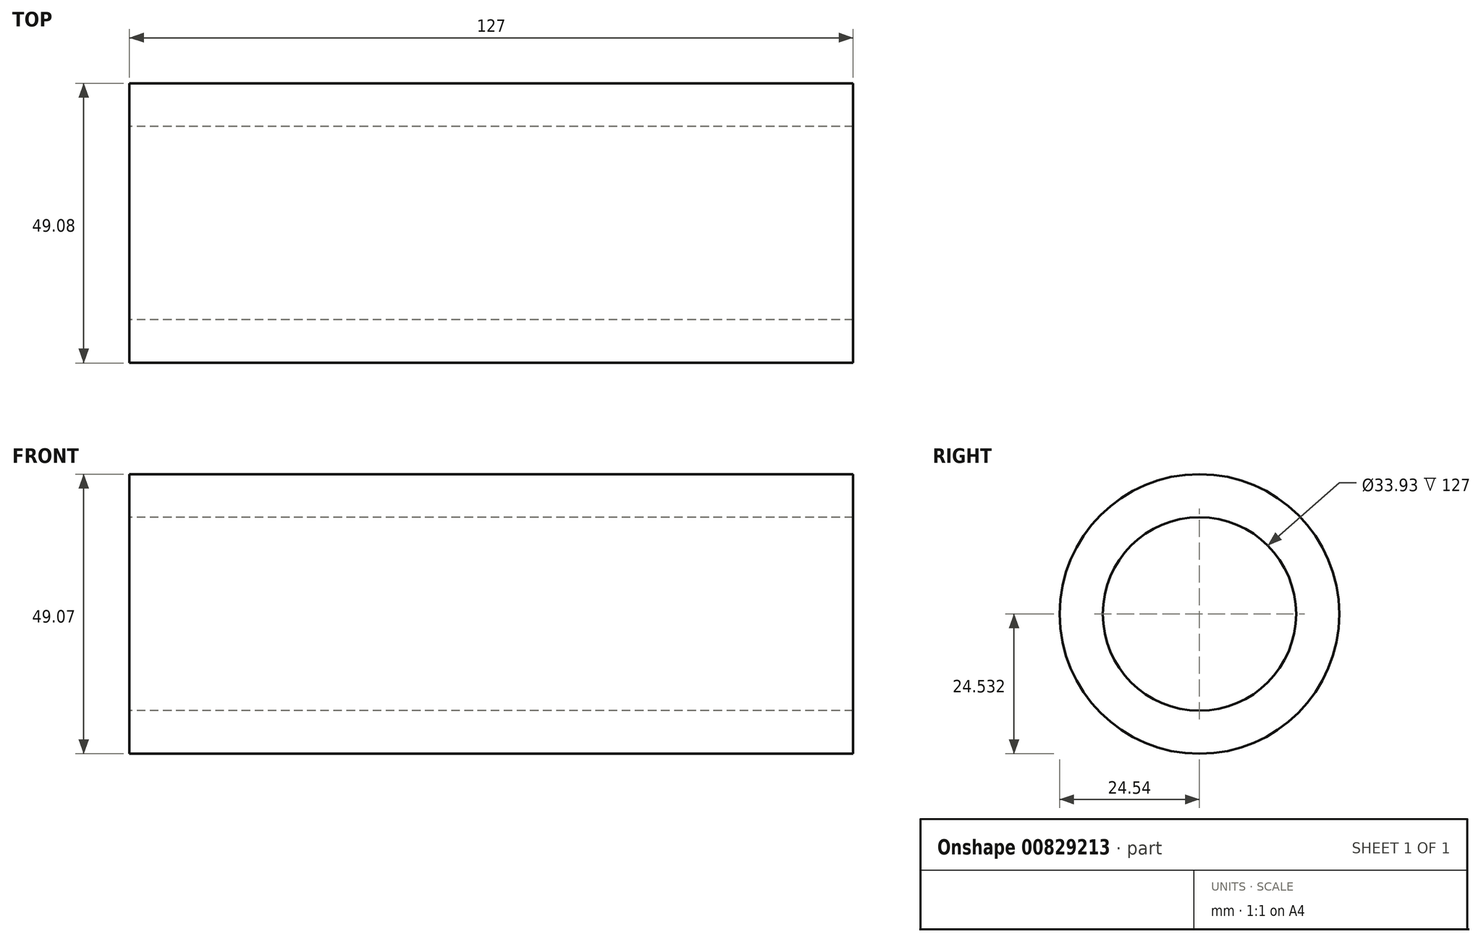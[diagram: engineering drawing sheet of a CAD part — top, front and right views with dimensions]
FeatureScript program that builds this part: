
annotation { "Feature Type Name" : "Feature", "Feature Type Description" : "" }
export const myFeature = defineFeature(function(context is Context, id is Id, definition is map)
    precondition{}
    {
        {
            var Q0;
            Q0=qCreatedBy(makeId("Right.planeOp"),FACE);
            var sketch = newSketch(context, id + "F0", { "sketchPlane" : qUnion([Q0])});
            skCircle(sketch, "E0", {"center": v(0, 35.03) * mm, "radius": 24.54 * mm});
            skCircle(sketch, "E1", {"center": v(0, 35.03) * mm, "radius": 16.97 * mm});
            skLineSegment(sketch, "E2", {"start": v(-24.07, 0) * mm, "end": v(-24.54, 35.03) * mm});
            skLineSegment(sketch, "E3", {"start": v(24.54, 35.03) * mm, "end": v(24.54, 0) * mm});
            skLineSegment(sketch, "E4", {"start": v(136.68, -13.56) * mm, "end": v(136.68, -22.93) * mm});
            skLineSegment(sketch, "E5", {"start": v(136.68, -22.93) * mm, "end": v(136.68, -18.25) * mm});
            skLineSegment(sketch, "E6", {"start": v(-24.07, 0) * mm, "end": v(24.54, 0) * mm});
            skSolve(sketch);
        }
        {
            var Q0;
            Q0=makeQuery(id+"F0.imprint","IMPRINT",FACE,{"disambiguationData":[TD([[makeQuery(id+"F0.imprint","IMPRINT",EDGE,{"derivedFrom":sQuery(id+"F0.wireOp",EDGE,"E1")}),-1.0]])]});
            extrude(context, id + "F1", {"entities" : qUnion([Q0]), "depth" : 127 * mm, "offsetDistance" : 25.4 * mm});
        }
    });
